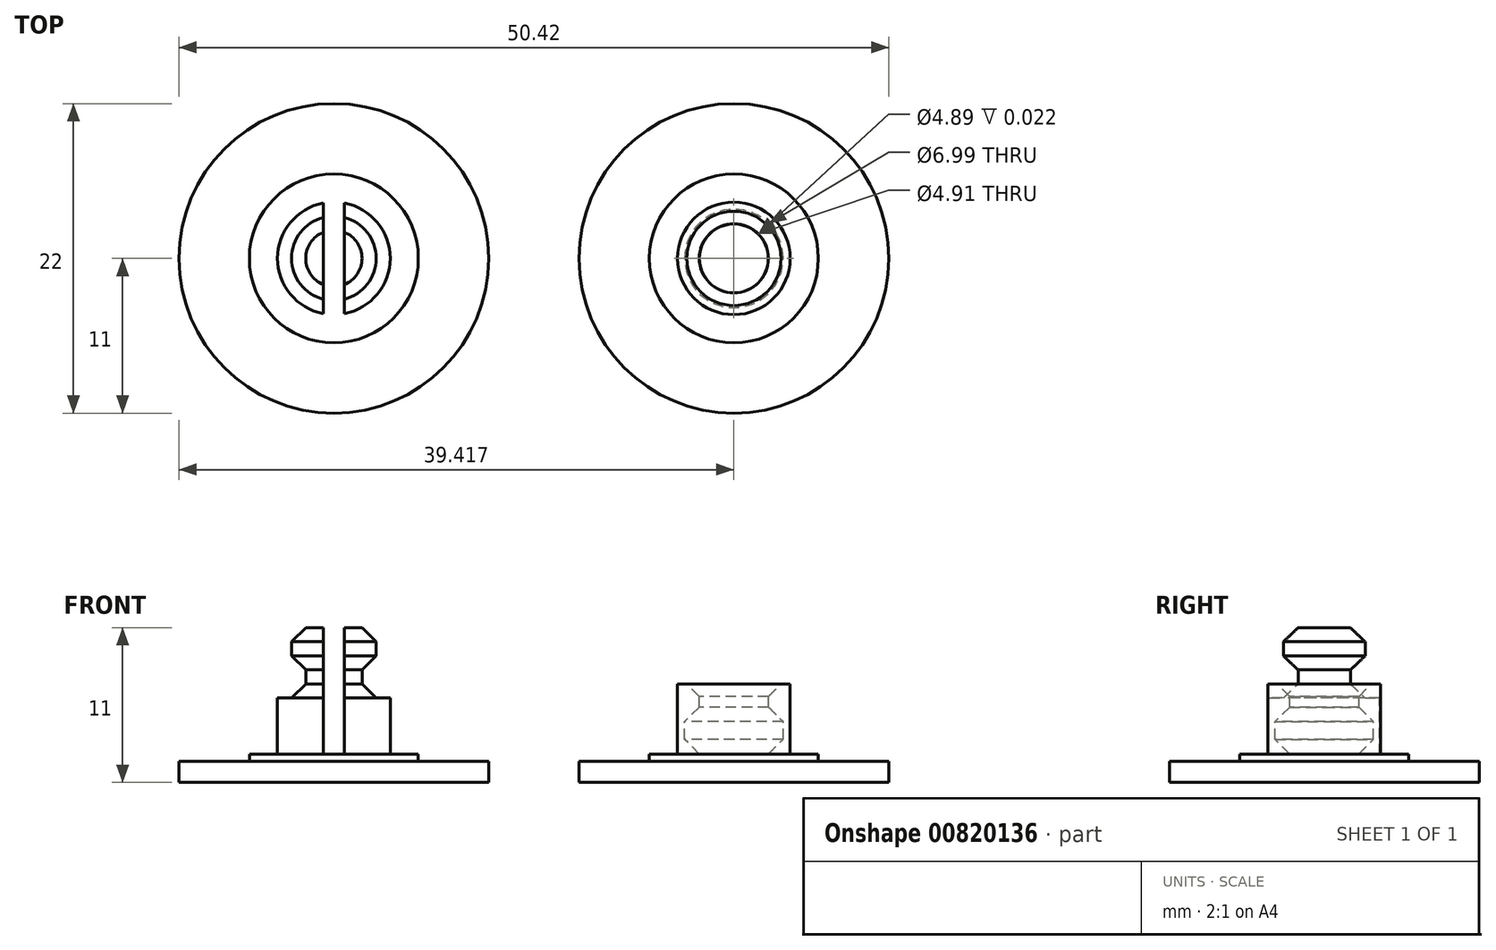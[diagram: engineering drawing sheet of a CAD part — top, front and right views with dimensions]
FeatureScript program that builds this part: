
annotation { "Feature Type Name" : "Feature", "Feature Type Description" : "" }
export const myFeature = defineFeature(function(context is Context, id is Id, definition is map)
    precondition{}
    {
        {
            var Q0;
            Q0=qCreatedBy(makeId("Front.planeOp"),FACE);
            var sketch = newSketch(context, id + "F0", { "sketchPlane" : qUnion([Q0])});
            skLineSegment(sketch, "E0.bottom", {"start": v(-14.2, 0) * mm, "end": v(-3.2, 0) * mm});
            skLineSegment(sketch, "E0.top", {"start": v(-14.2, 1.5) * mm, "end": v(-3.2, 1.5) * mm});
            skLineSegment(sketch, "E0.left", {"start": v(-14.2, 0) * mm, "end": v(-14.2, 1.5) * mm});
            skLineSegment(sketch, "E0.right", {"start": v(-3.2, 0) * mm, "end": v(-3.2, 1.5) * mm});
            skLineSegment(sketch, "E1.bottom", {"start": v(-14.2, 1.5) * mm, "end": v(-8.2, 1.5) * mm});
            skLineSegment(sketch, "E1.top", {"start": v(-14.2, 2) * mm, "end": v(-8.2, 2) * mm});
            skLineSegment(sketch, "E1.left", {"start": v(-14.2, 1.5) * mm, "end": v(-14.2, 2) * mm});
            skLineSegment(sketch, "E1.right", {"start": v(-8.2, 1.5) * mm, "end": v(-8.2, 2) * mm});
            skLineSegment(sketch, "E2", {"start": v(-11.2, 2) * mm, "end": v(-11.2, 11) * mm});
            skLineSegment(sketch, "E3", {"start": v(-11.2, 11) * mm, "end": v(-14.2, 11) * mm});
            skLineSegment(sketch, "E4", {"start": v(-14.2, 11) * mm, "end": v(-14.2, 2) * mm});
            skLineSegment(sketch, "E5.bottom", {"start": v(-13.46, 11) * mm, "end": v(-14.2, 11) * mm});
            skLineSegment(sketch, "E5.top", {"start": v(-13.46, 2) * mm, "end": v(-14.2, 2) * mm});
            skLineSegment(sketch, "E5.left", {"start": v(-13.46, 11) * mm, "end": v(-13.46, 2) * mm});
            skLineSegment(sketch, "E6", {"start": v(-12.2, 11) * mm, "end": v(-11.2, 10) * mm});
            skLineSegment(sketch, "E7", {"start": v(-11.2, 9) * mm, "end": v(-12.2, 8) * mm});
            skLineSegment(sketch, "E8", {"start": v(-12.2, 8) * mm, "end": v(-12.2, 7) * mm});
            skLineSegment(sketch, "E9", {"start": v(-12.2, 7) * mm, "end": v(-11.2, 6) * mm});
            skLineSegment(sketch, "E10.MirrorCS", {"start": v(-14.96, 11) * mm, "end": v(-14.2, 11) * mm});
            skLineSegment(sketch, "E11.MirrorCS", {"start": v(-14.96, 11) * mm, "end": v(-14.96, 2) * mm});
            skLineSegment(sketch, "E12.MirrorCS", {"start": v(-14.96, 2) * mm, "end": v(-14.2, 2) * mm});
            skLineSegment(sketch, "E13.bottom", {"start": v(-11.2, 6) * mm, "end": v(-10.2, 6) * mm});
            skLineSegment(sketch, "E13.top", {"start": v(-11.2, 2) * mm, "end": v(-10.2, 2) * mm});
            skLineSegment(sketch, "E13.left", {"start": v(-11.2, 6) * mm, "end": v(-11.2, 2) * mm});
            skLineSegment(sketch, "E13.right", {"start": v(-10.2, 6) * mm, "end": v(-10.2, 2) * mm});
            skLineSegment(sketch, "E14.MirrorCS", {"start": v(14.2, 0) * mm, "end": v(3.2, 0) * mm});
            skLineSegment(sketch, "E15.MirrorCS", {"start": v(14.2, 1.5) * mm, "end": v(3.2, 1.5) * mm});
            skLineSegment(sketch, "E16.MirrorCS", {"start": v(3.2, 0) * mm, "end": v(3.2, 1.5) * mm});
            skLineSegment(sketch, "E17.MirrorCS", {"start": v(14.2, 0) * mm, "end": v(14.2, 1.5) * mm});
            skLineSegment(sketch, "E18.MirrorCS", {"start": v(14.2, 2) * mm, "end": v(8.2, 2) * mm});
            skLineSegment(sketch, "E19.MirrorCS", {"start": v(8.2, 1.5) * mm, "end": v(8.2, 2) * mm});
            skLineSegment(sketch, "E20.MirrorCS", {"start": v(14.2, 1.5) * mm, "end": v(14.2, 2) * mm});
            skLineSegment(sketch, "E21", {"start": v(14.2, 2) * mm, "end": v(14.2, 7) * mm});
            skPoint(sketch, "E21.endSnap0", {"position": v(14.2, 0.75) * mm});
            skLineSegment(sketch, "E22.bottom", {"start": v(14.2, 7) * mm, "end": v(10.2, 7) * mm});
            skLineSegment(sketch, "E22.top", {"start": v(14.2, 2) * mm, "end": v(10.2, 2) * mm});
            skLineSegment(sketch, "E22.left", {"start": v(14.2, 7) * mm, "end": v(14.2, 2) * mm});
            skLineSegment(sketch, "E22.right", {"start": v(10.2, 7) * mm, "end": v(10.2, 2) * mm});
            skLineSegment(sketch, "E23", {"start": v(12.2, 2) * mm, "end": v(11.01, 3.2) * mm});
            skLineSegment(sketch, "E24", {"start": v(11.01, 4.2) * mm, "end": v(12.05, 5.23) * mm});
            skLineSegment(sketch, "E25", {"start": v(12.05, 5.23) * mm, "end": v(12.05, 6.23) * mm});
            skLineSegment(sketch, "E26", {"start": v(12.05, 6.23) * mm, "end": v(11.05, 7.23) * mm});
            skLineSegment(sketch, "E27", {"start": v(11.01, 3.2) * mm, "end": v(11.01, 4.2) * mm});
            skLineSegment(sketch, "E28.0", {"start": v(11.75, 6.1) * mm, "end": v(10.84, 7.02) * mm});
            skLineSegment(sketch, "E28.1", {"start": v(11.76, 2.02) * mm, "end": v(10.71, 3.07) * mm});
            skLineSegment(sketch, "E28.2", {"start": v(10.71, 3.07) * mm, "end": v(10.71, 4.32) * mm});
            skLineSegment(sketch, "E28.3", {"start": v(10.71, 4.32) * mm, "end": v(11.75, 5.36) * mm});
            skLineSegment(sketch, "E28.4", {"start": v(11.75, 5.36) * mm, "end": v(11.75, 6.1) * mm});
            skLineSegment(sketch, "E29", {"start": v(11.76, 2.02) * mm, "end": v(11.76, 1.82) * mm});
            skSolve(sketch);
        }
        {
            var Q0;
            Q0=makeQuery(id+"F0.imprint","IMPRINT",FACE,{"disambiguationData":[TD([[makeQuery(id+"F0.imprint","IMPRINT",EDGE,{"derivedFrom":sQuery(id+"F0.wireOp",EDGE,"E0.bottom")}),1.0]])]});
            var Q1;
            {var subQ5=sQuery(id+"F0.wireOp",EDGE,"E1.left");Q1=makeQuery(id+"F0.imprint","IMPRINT",FACE,{"disambiguationData":[TD([[makeQuery(id+"F0.imprint","IMPRINT",EDGE,{"derivedFrom":subQ5}),-1.0]])]});}
            var Q2;
            {var subQ2=sQuery(id+"F0.wireOp",EDGE,"E4");Q2=makeQuery(id+"F0.imprint","IMPRINT",FACE,{"disambiguationData":[TD([[makeQuery(id+"F0.imprint","IMPRINT",EDGE,{"derivedFrom":subQ2}),1.0]])]});}
            var Q3;
            {var subQ4=sQuery(id+"F0.wireOp",EDGE,"E13.bottom");Q3=makeQuery(id+"F0.imprint","IMPRINT",FACE,{"disambiguationData":[TD([[makeQuery(id+"F0.imprint","IMPRINT",EDGE,{"derivedFrom":subQ4}),-1.0]])]});}
            var Q4;
            {var subQ7=sQuery(id+"F0.wireOp",EDGE,"E5.left");Q4=makeQuery(id+"F0.imprint","IMPRINT",FACE,{"disambiguationData":[TD([[makeQuery(id+"F0.imprint","IMPRINT",EDGE,{"derivedFrom":subQ7}),1.0]])]});}
            var Q5;
            {var subQ5=sQuery(id+"F0.wireOp",EDGE,"E1.left");Q5=makeQuery(id+"F0.imprint","IMPRINT",FACE,{"disambiguationData":[TD([[makeQuery(id+"F0.imprint","IMPRINT",EDGE,{"derivedFrom":subQ5}),-1.0]])]});}
            var Q6;
            {var subQ2=sQuery(id+"F0.wireOp",EDGE,"E4");Q6=makeQuery(id+"F0.imprint","IMPRINT",FACE,{"disambiguationData":[TD([[makeQuery(id+"F0.imprint","IMPRINT",EDGE,{"derivedFrom":subQ2}),1.0]])]});}
            var Q7;
            Q7=sQuery(id+"F0.wireOp",EDGE,"E4");
            revolve(context, id + "F1", {"surfaceOperationType" : NewSurfaceOperationType.NEW, "entities" : qUnion([Q0, Q1, Q2, Q3, Q4, Q5, Q6]), "axis" : qUnion([Q7]), "revolveType" : RevolveType.FULL});
        }
        {
            var Q0;
            {var subQ2=sQuery(id+"F0.wireOp",EDGE,"E4");Q0=makeQuery(id+"F0.imprint","IMPRINT",FACE,{"disambiguationData":[TD([[makeQuery(id+"F0.imprint","IMPRINT",EDGE,{"derivedFrom":subQ2}),1.0]])]});}
            var Q1;
            Q1=makeQuery(id+"F0.imprint","IMPRINT",FACE,{"disambiguationData":[TD([[makeQuery(id+"F0.imprint","IMPRINT",EDGE,{"derivedFrom":sQuery(id+"F0.wireOp",EDGE,"E4")}),-1.0]])]});
            extrude(context, id + "F2", {"entities" : qUnion([Q0, Q1]), "operationType" : NewBodyOperationType.REMOVE, "endBound" : BoundingType.SYMMETRIC, "depth" : 25 * mm, "offsetDistance" : 25 * mm});
        }
        {
            var Q0;
            {var subQ4=sQuery(id+"F0.wireOp",EDGE,"E22.right");Q0=makeQuery(id+"F0.imprint","IMPRINT",FACE,{"disambiguationData":[TD([[makeQuery(id+"F0.imprint","IMPRINT",EDGE,{"derivedFrom":subQ4}),1.0]])]});}
            var Q1;
            {var subQ5=sQuery(id+"F0.wireOp",EDGE,"E19.MirrorCS");Q1=makeQuery(id+"F0.imprint","IMPRINT",FACE,{"disambiguationData":[TD([[makeQuery(id+"F0.imprint","IMPRINT",EDGE,{"derivedFrom":subQ5}),-1.0]])]});}
            var Q2;
            Q2=makeQuery(id+"F0.imprint","IMPRINT",FACE,{"disambiguationData":[TD([[makeQuery(id+"F0.imprint","IMPRINT",EDGE,{"derivedFrom":sQuery(id+"F0.wireOp",EDGE,"E14.MirrorCS")}),-1.0]])]});
            var Q3;
            Q3=sQuery(id+"F0.wireOp",EDGE,"E22.left");
            revolve(context, id + "F3", {"surfaceOperationType" : NewSurfaceOperationType.NEW, "entities" : qUnion([Q0, Q1, Q2]), "axis" : qUnion([Q3]), "revolveType" : RevolveType.FULL});
        }
    });
